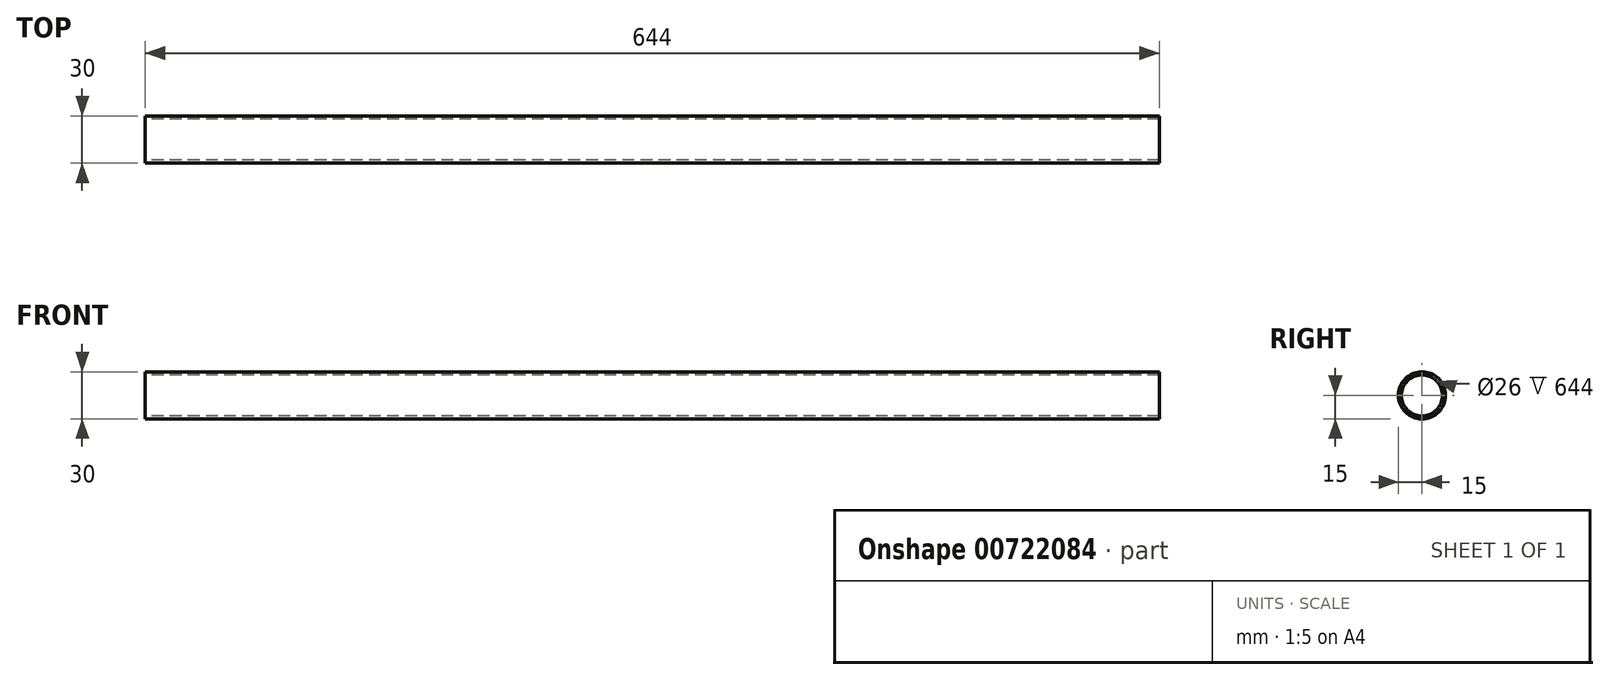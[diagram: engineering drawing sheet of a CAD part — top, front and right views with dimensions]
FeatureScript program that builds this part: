
annotation { "Feature Type Name" : "Feature", "Feature Type Description" : "" }
export const myFeature = defineFeature(function(context is Context, id is Id, definition is map)
    precondition{}
    {
        {
            var Q0;
            Q0=qCreatedBy(makeId("Right.planeOp"),FACE);
            var sketch = newSketch(context, id + "F0", { "sketchPlane" : qUnion([Q0])});
            skCircle(sketch, "E0", {"center": v(0, 0) * mm, "radius": 15 * mm});
            skCircle(sketch, "E1", {"center": v(0, 0) * mm, "radius": 13 * mm});
            skSolve(sketch);
        }
        {
            var Q0;
            Q0 = qSketchRegion(id + "F0", true);
            extrude(context, id + "F1", {"entities" : qUnion([Q0]), "depth" : 644 * mm, "offsetDistance" : 25 * mm});
        }
    });
